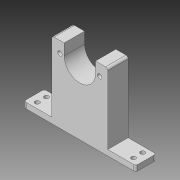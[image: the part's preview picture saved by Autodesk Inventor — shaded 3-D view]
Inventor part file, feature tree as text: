
AUTODESK INVENTOR PART (.ipt)
format: ipt  version: 2017 (Build 210142000, 142)  size: 154,112 bytes
history: native  units: mm
features: sketch x2, extrude x1, mirror x1, hole x1, fillet x1
ambient origin geometry x8: Origin, YZ Plane, XZ Plane, XY Plane, X Axis, Y Axis, Z Axis, Center Point
bodies: Solid1 (feature_tree)
feature tree (6):
  extrude  "Extrusion1"  Depth=50.0mm
  mirror  "Mirror1"
  hole  "Hole1"  [1 undecoded]
  fillet  "Fillet1"  Radius=4.0mm
  sketch  "Sketch1"  dims[d0=5.0mm d1=50.0mm]
  sketch  "Sketch2"  dims[d2=25.0mm d4=14.0mm d5=4.0mm d6=17.75mm d7=10.0mm d8=18.2mm d9=0.0mm d10=7.0mm d11=7.0mm d12=5.0mm d13=5.0mm d14=4.0mm d15=6.0mm d16=4.0mm d17=2.0mm d18=90.0deg d19=8.0mm d20=20.594885mm d21=2.0mm d22=50.0mm d23=6.0mm]
note: 1 required parameter value undecoded (feature->parameter linkage not recoverable at this tier; creation-order binding heuristic only, values carry confidence <= 0.55)
